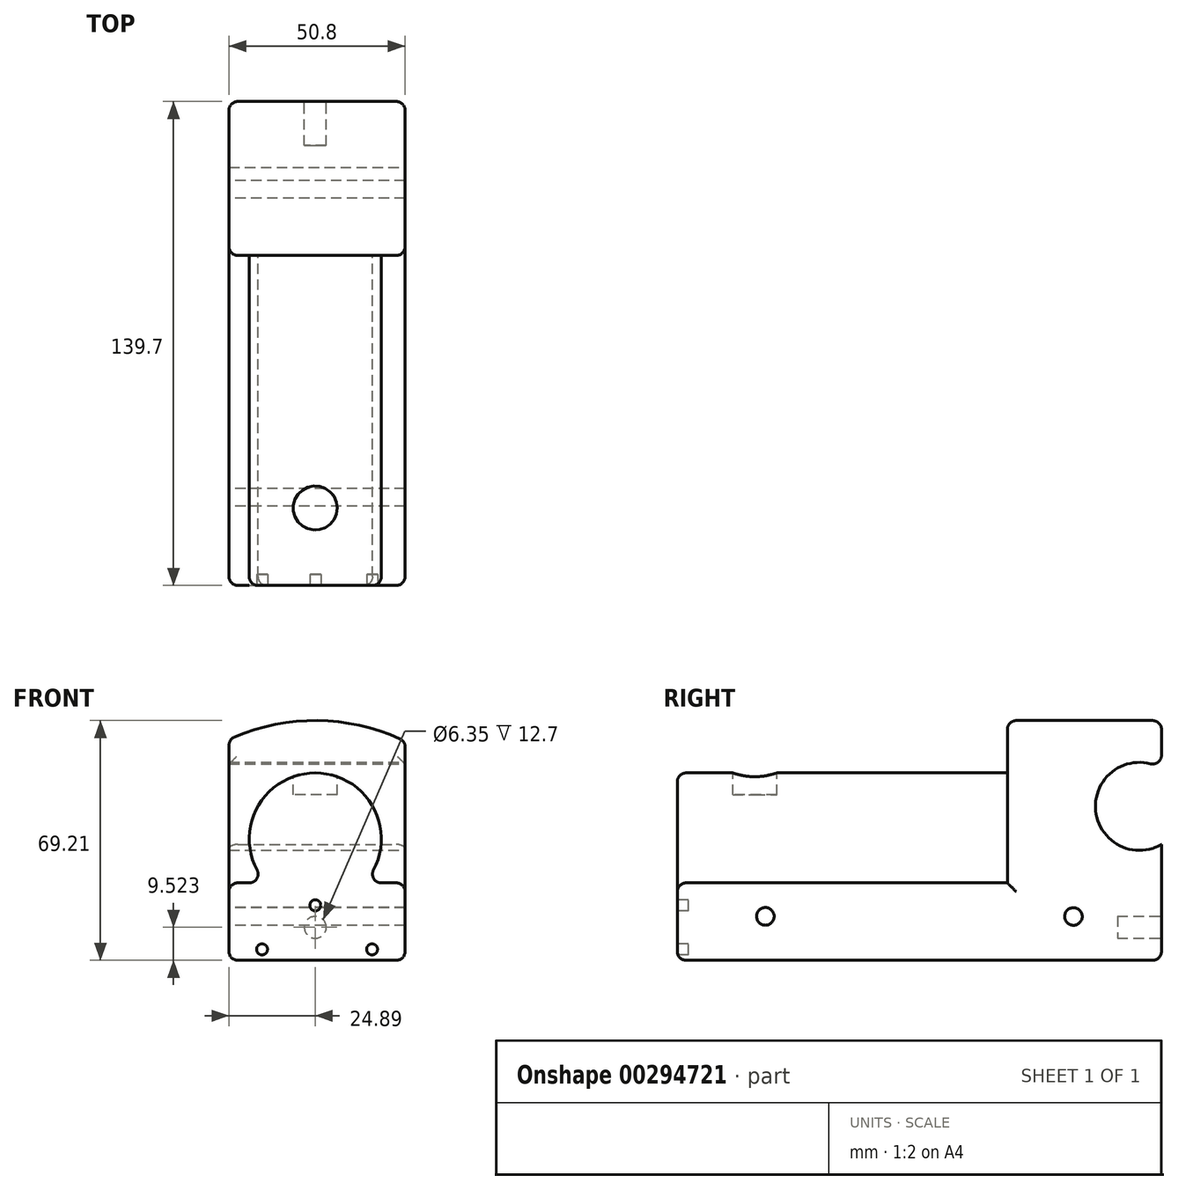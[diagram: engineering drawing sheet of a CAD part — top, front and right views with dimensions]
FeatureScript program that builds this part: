
annotation { "Feature Type Name" : "Feature", "Feature Type Description" : "" }
export const myFeature = defineFeature(function(context is Context, id is Id, definition is map)
    precondition{}
    {
        {
            var Q0;
            Q0=qCreatedBy(makeId("Front.planeOp"),FACE);
            var sketch = newSketch(context, id + "F0", { "sketchPlane" : qUnion([Q0])});
            skLineSegment(sketch, "E0.bottom", {"start": v(-24.89, 0) * mm, "end": v(-14.2, 0) * mm});
            skLineSegment(sketch, "E0.top", {"start": v(-24.89, -22.35) * mm, "end": v(25.91, -22.35) * mm});
            skLineSegment(sketch, "E0.left", {"start": v(-24.89, 0) * mm, "end": v(-24.89, -22.35) * mm});
            skLineSegment(sketch, "E0.right", {"start": v(25.91, 0) * mm, "end": v(25.91, -22.35) * mm});
            skArc(sketch, "E1", {"start": v(14.2, 0) * mm, "mid": v(0, 31.75) * mm, "end": v(-14.2, 0) * mm});
            skLineSegment(sketch, "E2.trimOffspring", {"start": v(14.2, 0) * mm, "end": v(25.91, 0) * mm});
            skSolve(sketch);
        }
        {
            var Q0;
            Q0=makeQuery(id+"F0.imprint","IMPRINT",FACE,{"disambiguationData":[TD([[makeQuery(id+"F0.imprint","IMPRINT",EDGE,{"derivedFrom":sQuery(id+"F0.wireOp",EDGE,"E0.bottom")}),-1.0]])]});
            extrude(context, id + "F1", {"entities" : qUnion([Q0]), "depth" : 95.25 * mm});
        }
        {
            var Q0;
            Q0=makeQuery(id+"F1.opExtrude","CAP_FACE",FACE,{"disambiguationData":[OSD([sQuery(id+"F0.wireOp",EDGE,"E0.bottom"),sQuery(id+"F0.wireOp",EDGE,"E0.top"),sQuery(id+"F0.wireOp",EDGE,"E0.left"),sQuery(id+"F0.wireOp",EDGE,"E0.right"),sQuery(id+"F0.wireOp",EDGE,"E1"),sQuery(id+"F0.wireOp",EDGE,"E2.trimOffspring")])],"isStart":true});
            var sketch = newSketch(context, id + "F2", { "sketchPlane" : qUnion([Q0])});
            skArc(sketch, "E3", {"start": v(24.89, 41.43) * mm, "mid": v(-0.57, 46.86) * mm, "end": v(-25.91, 40.95) * mm});
            skLineSegment(sketch, "E4", {"start": v(-25.91, 0) * mm, "end": v(-25.91, 40.95) * mm});
            skLineSegment(sketch, "E5", {"start": v(-25.91, 40.95) * mm, "end": v(-25.91, 40.95) * mm});
            skLineSegment(sketch, "E6", {"start": v(24.89, 0) * mm, "end": v(24.89, 41.43) * mm});
            skSolve(sketch);
        }
        {
            var Q0;
            Q0=makeQuery(id+"F2.imprint","IMPRINT",FACE,{"disambiguationData":[TD([[makeQuery(id+"F2.imprint","IMPRINT",EDGE,{"derivedFrom":sQuery(id+"F2.wireOp",EDGE,"E3")}),1.0]])]});
            var Q1;
            Q1=makeQuery(id+"F2.imprint","IMPRINT",FACE,{"disambiguationData":[TD([[makeQuery(id+"F2.imprint","IMPRINT",EDGE,{"derivedFrom":makeQuery(id+"F1.opExtrude","CAP_EDGE",EDGE,{"disambiguationData":[OSD([sQuery(id+"F0.wireOp",EDGE,"E0.bottom")])],"isStart":true})}),1.0]])]});
            extrude(context, id + "F3", {"entities" : qUnion([Q0, Q1]), "operationType" : NewBodyOperationType.ADD, "depth" : 44.45 * mm});
        }
        {
            var Q0;
            {var subQ0=sQuery(id+"F0.wireOp",EDGE,"E0.right");Q0=makeQuery(id+"F3.boolean.opBoolean","MERGE",FACE,{"derivedFrom":[makeQuery(id+"F1.opExtrude","SWEPT_FACE",FACE,{"disambiguationData":[OSD([subQ0])]}),makeQuery(id+"F3.opExtrude","SWEPT_FACE",FACE,{"disambiguationData":[OSD([subQ0,sQuery(id+"F2.wireOp",EDGE,"E4")])]})]});}
            var sketch = newSketch(context, id + "F4", { "sketchPlane" : qUnion([Q0])});
            skArc(sketch, "E7", {"start": v(44.45, 33.1) * mm, "mid": v(25.4, 22.1) * mm, "end": v(44.45, 11.1) * mm});
            skLineSegment(sketch, "E8", {"start": v(44.45, 33.1) * mm, "end": v(44.45, 11.1) * mm});
            skPoint(sketch, "E8.endSnap0", {"position": v(44.45, 9.3) * mm});
            skSolve(sketch);
        }
        {
            var Q0;
            Q0=makeQuery(id+"F4.imprint","IMPRINT",FACE,{"disambiguationData":[TD([[makeQuery(id+"F4.imprint","IMPRINT",EDGE,{"derivedFrom":sQuery(id+"F4.wireOp",EDGE,"E7")}),1.0]])]});
            extrude(context, id + "F5", {"entities" : qUnion([Q0]), "operationType" : NewBodyOperationType.REMOVE, "oppositeDirection" : true, "depth" : 50.8 * mm});
        }
        {
            var Q0;
            Q0=makeQuery(id+"F1.opExtrude","CAP_FACE",FACE,{"disambiguationData":[OSD([sQuery(id+"F0.wireOp",EDGE,"E0.bottom"),sQuery(id+"F0.wireOp",EDGE,"E0.top"),sQuery(id+"F0.wireOp",EDGE,"E0.left"),sQuery(id+"F0.wireOp",EDGE,"E0.right"),sQuery(id+"F0.wireOp",EDGE,"E1"),sQuery(id+"F0.wireOp",EDGE,"E2.trimOffspring")])],"isStart":false});
            var sketch = newSketch(context, id + "F6", { "sketchPlane" : qUnion([Q0])});
            skCircle(sketch, "E9", {"center": v(-15.36, -19.18) * mm, "radius": 1.59 * mm});
            skCircle(sketch, "E10", {"center": v(0, -6.48) * mm, "radius": 1.59 * mm});
            skCircle(sketch, "E11", {"center": v(16.39, -19.18) * mm, "radius": 1.59 * mm});
            skLineSegment(sketch, "E12.0", {"start": v(-24.89, -22.35) * mm, "end": v(25.91, -22.35) * mm});
            skSolve(sketch);
        }
        {
            var Q0;
            Q0=makeQuery(id+"F6.imprint","IMPRINT",FACE,{"disambiguationData":[TD([[makeQuery(id+"F6.imprint","IMPRINT",EDGE,{"derivedFrom":sQuery(id+"F6.wireOp",EDGE,"E10")}),1.0]])]});
            var Q1;
            Q1=makeQuery(id+"F6.imprint","IMPRINT",FACE,{"disambiguationData":[TD([[makeQuery(id+"F6.imprint","IMPRINT",EDGE,{"derivedFrom":sQuery(id+"F6.wireOp",EDGE,"E9")}),1.0]])]});
            var Q2;
            Q2=makeQuery(id+"F6.imprint","IMPRINT",FACE,{"disambiguationData":[TD([[makeQuery(id+"F6.imprint","IMPRINT",EDGE,{"derivedFrom":sQuery(id+"F6.wireOp",EDGE,"E11")}),1.0]])]});
            extrude(context, id + "F7", {"entities" : qUnion([Q0, Q1, Q2]), "operationType" : NewBodyOperationType.REMOVE, "oppositeDirection" : true, "depth" : 3.17 * mm});
        }
        {
            var Q0;
            {var subQ0=sQuery(id+"F0.wireOp",EDGE,"E0.right");Q0=makeQuery(id+"F3.boolean.opBoolean","MERGE",FACE,{"derivedFrom":[makeQuery(id+"F1.opExtrude","SWEPT_FACE",FACE,{"disambiguationData":[OSD([subQ0])]}),makeQuery(id+"F3.opExtrude","SWEPT_FACE",FACE,{"disambiguationData":[OSD([subQ0,sQuery(id+"F2.wireOp",EDGE,"E4")])]})]});}
            var sketch = newSketch(context, id + "F8", { "sketchPlane" : qUnion([Q0])});
            skPoint(sketch, "E13", {"position": v(-69.85, -9.65) * mm});
            skPoint(sketch, "E14", {"position": v(19.05, -9.7) * mm});
            skSolve(sketch);
        }
        {
            var Q0;
            Q0=sQuery(id+"F8.wireOp",VERTEX,"E13");
            var Q1;
            Q1=sQuery(id+"F8.wireOp",VERTEX,"E14");
            var Q2;
            Q2=makeQuery(id+"F1.opExtrude","SWEPT_BODY",BODY,{"disambiguationData":[OSD([sQuery(id+"F0.wireOp",EDGE,"E0.bottom"),sQuery(id+"F0.wireOp",EDGE,"E0.top"),sQuery(id+"F0.wireOp",EDGE,"E0.left"),sQuery(id+"F0.wireOp",EDGE,"E0.right"),sQuery(id+"F0.wireOp",EDGE,"E1"),sQuery(id+"F0.wireOp",EDGE,"E2.trimOffspring")])]});
            hole(context, id + "F9", {"style" : HoleStyle.SIMPLE, "endStyle" : HoleEndStyle.THROUGH, "standardTappedOrClearance" : lookupTablePath({ "standard" : "ANSI", "fit" : "Normal (ASME)", "engagement" : "75%", "pitch" : "20 tpi", "size" : "1/4", "type" : "Tapped" }), "standardBlindInLast" : lookupTablePath({ "fit" : "Free", "standard" : "ANSI", "engagement" : "75%", "pitch" : "20 tpi", "size" : "1/4", "type" : "Tapped" }), "holeDiameter" : 5.1 * mm, "showTappedDepth" : true, "tappedDepth" : 50.8 * mm, "tapClearance" : 3, "locations" : qUnion([Q0, Q1]), "scope" : qUnion([Q2]), "majorDiameter" : 6.35 * mm});
        }
        {
            var Q0;
            Q0=qCreatedBy(makeId("Top.planeOp"),FACE);
            cPlane(context, id + "F10", {"entities" : qUnion([Q0]), "cplaneType" : CPlaneType.OFFSET, "offset" : 31.75 * mm, "width" : 152.4 * mm, "height" : 152.4 * mm});
        }
        {
            var Q0;
            Q0=qCreatedBy(id+"F10.planeOp",FACE);
            var sketch = newSketch(context, id + "F11", { "sketchPlane" : qUnion([Q0])});
            skCircle(sketch, "E15", {"center": v(0, -72.9) * mm, "radius": 6.35 * mm});
            skSolve(sketch);
        }
        {
            var Q0;
            Q0=makeQuery(id+"F11.imprint","IMPRINT",FACE,{"disambiguationData":[TD([[makeQuery(id+"F11.imprint","IMPRINT",EDGE,{"derivedFrom":sQuery(id+"F11.wireOp",EDGE,"E15")}),1.0]])]});
            extrude(context, id + "F12", {"entities" : qUnion([Q0]), "operationType" : NewBodyOperationType.REMOVE, "oppositeDirection" : true, "depth" : 6.35 * mm});
        }
        {
            var Q0;
            {var subQ0=sQuery(id+"F2.wireOp",EDGE,"E4");var subQ1=sQuery(id+"F0.wireOp",EDGE,"E0.right");var subQ2=sQuery(id+"F0.wireOp",EDGE,"E0.left");var subQ3=sQuery(id+"F2.wireOp",EDGE,"E6");var subQ4=sQuery(id+"F0.wireOp",EDGE,"E0.top");Q0=makeQuery(id+"F5.boolean.opBoolean","SPLIT",FACE,{"disambiguationData":[TD([makeQuery(id+"F1.opExtrude","SWEPT_FACE",FACE,{"disambiguationData":[OSD([subQ4])]})])],"derivedFrom":makeQuery(id+"F3.opExtrude","CAP_FACE",FACE,{"disambiguationData":[OSD([subQ4,subQ2,subQ1,sQuery(id+"F2.wireOp",EDGE,"E3"),subQ0,subQ3])],"isStart":false})});}
            var sketch = newSketch(context, id + "F13", { "sketchPlane" : qUnion([Q0])});
            skCircle(sketch, "E16", {"center": v(0, -12.83) * mm, "radius": 3.18 * mm});
            skSolve(sketch);
        }
        {
            var Q0;
            Q0=makeQuery(id+"F13.imprint","IMPRINT",FACE,{"disambiguationData":[TD([[makeQuery(id+"F13.imprint","IMPRINT",EDGE,{"derivedFrom":sQuery(id+"F13.wireOp",EDGE,"E16")}),1.0]])]});
            extrude(context, id + "F14", {"entities" : qUnion([Q0]), "operationType" : NewBodyOperationType.REMOVE, "oppositeDirection" : true, "depth" : 12.7 * mm});
        }
        {
            var Q0;
            {var subQ0=sQuery(id+"F2.wireOp",EDGE,"E4");var subQ1=sQuery(id+"F0.wireOp",EDGE,"E0.right");var subQ2=sQuery(id+"F0.wireOp",EDGE,"E0.left");var subQ3=sQuery(id+"F2.wireOp",EDGE,"E3");var subQ4=sQuery(id+"F2.wireOp",EDGE,"E6");Q0=makeQuery(id+"F5.boolean.opBoolean","SPLIT",FACE,{"disambiguationData":[TD([makeQuery(id+"F3.opExtrude","SWEPT_FACE",FACE,{"disambiguationData":[OSD([subQ3])]})])],"derivedFrom":makeQuery(id+"F3.opExtrude","CAP_FACE",FACE,{"disambiguationData":[OSD([sQuery(id+"F0.wireOp",EDGE,"E0.top"),subQ2,subQ1,subQ3,subQ0,subQ4])],"isStart":false})});}
            var Q1;
            Q1=makeQuery(id+"F3.opExtrude","SWEPT_FACE",FACE,{"disambiguationData":[OSD([sQuery(id+"F2.wireOp",EDGE,"E3")])]});
            var Q2;
            Q2=makeQuery(id+"F5.boolean.opBoolean","COPY",EDGE,{"derivedFrom":makeQuery(id+"F5.opExtrude","CAP_EDGE",EDGE,{"disambiguationData":[OSD([sQuery(id+"F4.wireOp",EDGE,"E7")])],"isStart":false})});
            var Q3;
            Q3=makeQuery(id+"F3.opExtrude","CAP_EDGE",EDGE,{"disambiguationData":[OSD([sQuery(id+"F0.wireOp",EDGE,"E0.left"),sQuery(id+"F2.wireOp",EDGE,"E6")])],"isStart":true});
            var Q4;
            Q4=makeQuery(id+"F1.opExtrude","SWEPT_EDGE",EDGE,{"disambiguationData":[OSD([sQuery(id+"F0.wireOp",EDGE,"E0.bottom"),sQuery(id+"F0.wireOp",EDGE,"E0.left")])]});
            var Q5;
            {var subQ0=sQuery(id+"F0.wireOp",EDGE,"E0.left");var subQ1=sQuery(id+"F0.wireOp",EDGE,"E0.top");Q5=makeQuery(id+"F3.boolean.opBoolean","MERGE",EDGE,{"derivedFrom":[makeQuery(id+"F1.opExtrude","SWEPT_EDGE",EDGE,{"disambiguationData":[OSD([subQ1,subQ0])]}),makeQuery(id+"F3.opExtrude","SWEPT_EDGE",EDGE,{"disambiguationData":[OSD([subQ1,subQ0])]})]});}
            var Q6;
            {var subQ0=sQuery(id+"F2.wireOp",EDGE,"E6");var subQ1=sQuery(id+"F0.wireOp",EDGE,"E0.left");var subQ2=sQuery(id+"F0.wireOp",EDGE,"E0.top");Q6=makeQuery(id+"F5.boolean.opBoolean","SPLIT",EDGE,{"disambiguationData":[TD([makeQuery(id+"F1.opExtrude","SWEPT_FACE",FACE,{"disambiguationData":[OSD([subQ2])]})])],"derivedFrom":makeQuery(id+"F3.opExtrude","CAP_EDGE",EDGE,{"disambiguationData":[OSD([subQ1,subQ0])],"isStart":false})});}
            var Q7;
            {var subQ0=sQuery(id+"F4.wireOp",EDGE,"E8");var subQ1=sQuery(id+"F4.wireOp",EDGE,"E7");var subQ2=sQuery(id+"F2.wireOp",EDGE,"E4");var subQ3=sQuery(id+"F0.wireOp",EDGE,"E0.right");Q7=makeQuery(id+"F5.boolean.opBoolean","COPY",EDGE,{"derivedFrom":makeQuery(id+"F5.opExtrude","SWEPT_EDGE",EDGE,{"disambiguationData":[OSD([subQ3,subQ2,subQ1,subQ0]),TDD([makeQuery(id+"F4.imprint","INTERSECT",VERTEX,{"disambiguationData":[OD(1.0)],"derivedFrom":[makeQuery(id+"F3.opExtrude","CAP_EDGE",EDGE,{"disambiguationData":[OSD([subQ3,subQ2])],"isStart":false}),subQ1,subQ0]})])]})});}
            var Q8;
            {var subQ0=sQuery(id+"F2.wireOp",EDGE,"E4");var subQ1=sQuery(id+"F0.wireOp",EDGE,"E0.right");var subQ2=sQuery(id+"F0.wireOp",EDGE,"E0.top");Q8=makeQuery(id+"F5.boolean.opBoolean","SPLIT",EDGE,{"disambiguationData":[TD([makeQuery(id+"F1.opExtrude","SWEPT_FACE",FACE,{"disambiguationData":[OSD([subQ2])]})])],"derivedFrom":makeQuery(id+"F3.opExtrude","CAP_EDGE",EDGE,{"disambiguationData":[OSD([subQ1,subQ0])],"isStart":false})});}
            var Q9;
            Q9=makeQuery(id+"F3.opExtrude","CAP_EDGE",EDGE,{"disambiguationData":[OSD([sQuery(id+"F0.wireOp",EDGE,"E0.top")])],"isStart":false});
            var Q10;
            Q10=makeQuery(id+"F3.opExtrude","CAP_EDGE",EDGE,{"disambiguationData":[OSD([sQuery(id+"F0.wireOp",EDGE,"E0.right"),sQuery(id+"F2.wireOp",EDGE,"E4")])],"isStart":true});
            var Q11;
            Q11=makeQuery(id+"F1.opExtrude","SWEPT_EDGE",EDGE,{"disambiguationData":[OSD([sQuery(id+"F0.wireOp",EDGE,"E0.right"),sQuery(id+"F0.wireOp",EDGE,"E2.trimOffspring")])]});
            var Q12;
            Q12=makeQuery(id+"F1.opExtrude","CAP_EDGE",EDGE,{"disambiguationData":[OSD([sQuery(id+"F0.wireOp",EDGE,"E0.right")])],"isStart":false});
            var Q13;
            {var subQ0=sQuery(id+"F0.wireOp",EDGE,"E0.right");var subQ1=sQuery(id+"F0.wireOp",EDGE,"E0.top");Q13=makeQuery(id+"F3.boolean.opBoolean","MERGE",EDGE,{"derivedFrom":[makeQuery(id+"F1.opExtrude","SWEPT_EDGE",EDGE,{"disambiguationData":[OSD([subQ1,subQ0])]}),makeQuery(id+"F3.opExtrude","SWEPT_EDGE",EDGE,{"disambiguationData":[OSD([subQ1,subQ0])]})]});}
            var Q14;
            Q14=makeQuery(id+"F1.opExtrude","CAP_EDGE",EDGE,{"disambiguationData":[OSD([sQuery(id+"F0.wireOp",EDGE,"E1")])],"isStart":false});
            var Q15;
            Q15=makeQuery(id+"F1.opExtrude","CAP_EDGE",EDGE,{"disambiguationData":[OSD([sQuery(id+"F0.wireOp",EDGE,"E2.trimOffspring")])],"isStart":false});
            var Q16;
            Q16=makeQuery(id+"F1.opExtrude","CAP_EDGE",EDGE,{"disambiguationData":[OSD([sQuery(id+"F0.wireOp",EDGE,"E0.bottom")])],"isStart":false});
            var Q17;
            Q17=makeQuery(id+"F1.opExtrude","CAP_EDGE",EDGE,{"disambiguationData":[OSD([sQuery(id+"F0.wireOp",EDGE,"E0.left")])],"isStart":false});
            var Q18;
            Q18=makeQuery(id+"F1.opExtrude","CAP_EDGE",EDGE,{"disambiguationData":[OSD([sQuery(id+"F0.wireOp",EDGE,"E0.top")])],"isStart":false});
            var Q19;
            Q19=makeQuery(id+"F1.opExtrude","SWEPT_EDGE",EDGE,{"disambiguationData":[OSD([sQuery(id+"F0.wireOp",EDGE,"E1"),sQuery(id+"F0.wireOp",EDGE,"E2.trimOffspring")])]});
            var Q20;
            Q20=makeQuery(id+"F1.opExtrude","SWEPT_EDGE",EDGE,{"disambiguationData":[OSD([sQuery(id+"F0.wireOp",EDGE,"E0.bottom"),sQuery(id+"F0.wireOp",EDGE,"E1")])]});
            var Q21;
            Q21=makeQuery(id+"F5.boolean.opBoolean","COPY",EDGE,{"derivedFrom":makeQuery(id+"F5.opExtrude","CAP_EDGE",EDGE,{"disambiguationData":[OSD([sQuery(id+"F4.wireOp",EDGE,"E7")])],"isStart":true})});
            var Q22;
            Q22=makeQuery(id+"F1.opExtrude","CAP_EDGE",EDGE,{"disambiguationData":[OSD([sQuery(id+"F0.wireOp",EDGE,"E1")])],"isStart":true});
            fillet(context, id + "F15", {"entities" : qUnion([Q0, Q1, Q2, Q3, Q4, Q5, Q6, Q7, Q8, Q9, Q10, Q11, Q12, Q13, Q14, Q15, Q16, Q17, Q18, Q19, Q20, Q21, Q22]), "radius" : 2.54 * mm, "tangentPropagation" : true, "allowEdgeOverflow" : false});
        }
    });
